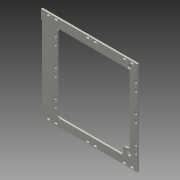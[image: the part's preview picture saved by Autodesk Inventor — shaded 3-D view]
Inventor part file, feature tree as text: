
AUTODESK INVENTOR PART (.ipt)
format: ipt  version: 2013 (Build 170138000, 138)  size: 284,160 bytes
history: native  units: mm
features: extrude x1, sketch x1
ambient origin geometry x8: Origin, YZ Plane, XZ Plane, XY Plane, X Axis, Y Axis, Z Axis, Center Point
bodies: Solid1 (feature_tree)
feature tree (2):
  extrude  "Extrusion1"  Depth=354.4mm
  sketch  "Sketch1"  dims[d0=344.1mm d2=354.4mm d3=9.4mm d4=0.0mm d5=3.0mm d6=35.0mm d7=135.0deg d8=40.0mm d9=6.4mm d10=3.2mm d11=12.0mm d12=7.8mm d13=7.8mm d14=12.0mm d15=12.0mm d16=7.8mm d17=7.8mm d18=12.0mm d19=12.0mm d20=7.8mm d21=7.8mm d22=12.0mm d23=135.0mm d24=144.4mm d25=6.4mm d26=3.2mm d27=6.2mm d28=35.0mm d29=3.0mm d30=6.2mm d31=6.4mm d32=3.2mm d33=12.0mm d34=7.8mm d35=7.8mm d36=12.0mm d37=12.0mm d38=7.8mm d39=7.8mm d40=12.0mm d41=12.0mm d42=7.8mm d43=7.8mm d44=12.0mm d46=6.2mm d47=100.0mm d48=100.0mm d49=53.2mm d50=6.4mm d51=3.2mm d52=16.1mm d53=11.0mm d54=11.0mm d55=21.7mm d56=31.0mm d57=43.4mm d58=28.0mm d59=32.0mm d60=56.4mm d61=28.0mm d62=25.0mm d63=30.0mm d64=10.0mm d65=6.0mm d66=0.0mm d67=162.65mm]
